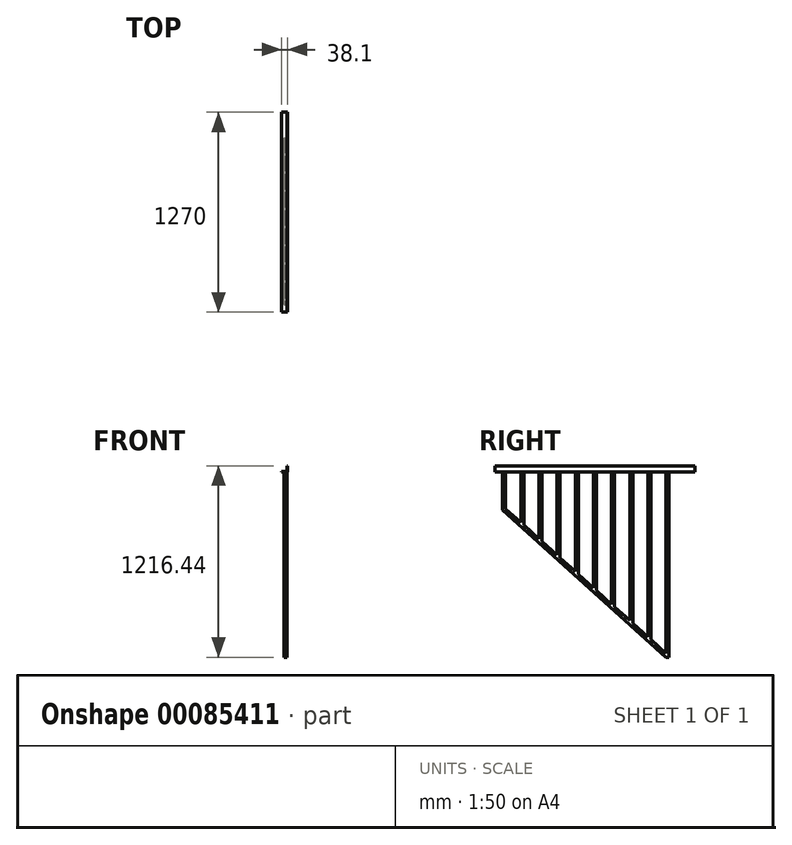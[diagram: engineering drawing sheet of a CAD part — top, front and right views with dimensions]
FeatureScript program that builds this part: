
annotation { "Feature Type Name" : "Feature", "Feature Type Description" : "" }
export const myFeature = defineFeature(function(context is Context, id is Id, definition is map)
    precondition{}
    {
        {
            var Q0;
            Q0=qCreatedBy(makeId("Right.planeOp"),FACE);
            var sketch = newSketch(context, id + "F2", { "sketchPlane" : qUnion([Q0])});
            skLineSegment(sketch, "E0", {"start": v(-1015.88, 696.31) * mm, "end": v(-1015.88, 601.06) * mm});
            skLineSegment(sketch, "E1", {"start": v(-1015.88, 601.06) * mm, "end": v(-790.45, 601.06) * mm});
            skLineSegment(sketch, "E2", {"start": v(-790.45, 601.06) * mm, "end": v(-790.45, 601.06) * mm});
            skLineSegment(sketch, "E3", {"start": v(-790.45, 601.06) * mm, "end": v(-790.45, 397.86) * mm});
            skLineSegment(sketch, "E4", {"start": v(-790.45, 397.86) * mm, "end": v(-565.03, 397.86) * mm});
            skLineSegment(sketch, "E5", {"start": v(-565.03, 397.86) * mm, "end": v(-565.03, 194.66) * mm});
            skLineSegment(sketch, "E6", {"start": v(-565.03, 194.66) * mm, "end": v(-339.6, 194.66) * mm});
            skLineSegment(sketch, "E7", {"start": v(-339.6, 194.66) * mm, "end": v(-339.6, -14.89) * mm});
            skLineSegment(sketch, "E8", {"start": v(-339.6, -14.89) * mm, "end": v(-339.6, -14.89) * mm});
            skLineSegment(sketch, "E9", {"start": v(-114.18, -14.89) * mm, "end": v(-339.6, -14.89) * mm});
            skLineSegment(sketch, "E10", {"start": v(-114.18, -14.89) * mm, "end": v(-114.18, -218.09) * mm});
            skLineSegment(sketch, "E11", {"start": v(-114.18, -218.09) * mm, "end": v(114.42, -218.09) * mm});
            skLineSegment(sketch, "E12", {"start": v(114.42, -218.09) * mm, "end": v(114.42, -421.29) * mm});
            skLineSegment(sketch, "E13", {"start": v(114.42, -421.29) * mm, "end": v(343.02, -421.29) * mm});
            skLineSegment(sketch, "E14", {"start": v(-1015.88, 696.31) * mm, "end": v(1087.24, 696.31) * mm});
            skLineSegment(sketch, "E15", {"start": v(343.02, -421.29) * mm, "end": v(343.02, -624.49) * mm});
            skLineSegment(sketch, "E16", {"start": v(343.02, -624.49) * mm, "end": v(571.62, -624.49) * mm});
            skLineSegment(sketch, "E17", {"start": v(571.62, -624.49) * mm, "end": v(571.62, -827.69) * mm});
            skLineSegment(sketch, "E18", {"start": v(571.62, -827.69) * mm, "end": v(806.57, -827.69) * mm});
            skLineSegment(sketch, "E19", {"start": v(806.57, -827.69) * mm, "end": v(806.57, -1030.89) * mm});
            skLineSegment(sketch, "E20", {"start": v(806.57, -1030.89) * mm, "end": v(1035.17, -1030.89) * mm});
            skLineSegment(sketch, "E21", {"start": v(774.82, -827.69) * mm, "end": v(774.82, 696.31) * mm});
            skLineSegment(sketch, "E22", {"start": v(863.72, 696.31) * mm, "end": v(863.72, -1030.89) * mm});
            skLineSegment(sketch, "E23", {"start": v(1035.17, -1030.89) * mm, "end": v(1035.17, -1234.09) * mm});
            skLineSegment(sketch, "E24", {"start": v(1035.17, -1234.09) * mm, "end": v(1503, -1234.09) * mm});
            skLineSegment(sketch, "E25", {"start": v(806.57, -827.69) * mm, "end": v(1035.17, -1030.89) * mm, "construction": true});
            skLineSegment(sketch, "E26", {"start": v(971.74, -1030.89) * mm, "end": v(806.57, -884.07) * mm, "construction": true});
            skCircle(sketch, "E27", {"center": v(857.37, -980.09) * mm, "radius": 50.8 * mm, "construction": true});
            skLineSegment(sketch, "E28", {"start": v(806.57, -1030.89) * mm, "end": v(893.3, -944.17) * mm, "construction": true});
            skSolve(sketch);
        }
        {
            var Q0;
            Q0=qCreatedBy(makeId("Front.planeOp"),FACE);
            var sketch = newSketch(context, id + "F0", { "sketchPlane" : qUnion([Q0])});
            skLineSegment(sketch, "E29", {"start": v(3.17, 731.24) * mm, "end": v(3.18, 693.14) * mm});
            skLineSegment(sketch, "E30", {"start": v(3.18, 693.14) * mm, "end": v(-34.93, 693.14) * mm});
            skLineSegment(sketch, "E31", {"start": v(-34.93, 693.14) * mm, "end": v(-34.93, 696.31) * mm});
            skLineSegment(sketch, "E32", {"start": v(-34.93, 696.31) * mm, "end": v(0, 696.31) * mm});
            skLineSegment(sketch, "E33", {"start": v(0, 696.31) * mm, "end": v(0, 731.24) * mm});
            skLineSegment(sketch, "E34", {"start": v(0, 731.24) * mm, "end": v(3.17, 731.24) * mm});
            skSolve(sketch);
        }
        {
            var Q0;
            Q0=makeQuery(id+"F0.imprint","IMPRINT",FACE,{"disambiguationData":[TD([[makeQuery(id+"F0.imprint","IMPRINT",EDGE,{"derivedFrom":sQuery(id+"F0.wireOp",EDGE,"E29")}),-1.0]])]});
            extrude(context, id + "F1", {"entities" : qUnion([Q0]), "depth" : 762 * mm, "hasSecondDirection" : true, "secondDirectionOppositeDirection" : true, "secondDirectionDepth" : 508 * mm});
        }
        {
            var Q0;
            Q0=qCreatedBy(makeId("Right.planeOp"),FACE);
            var sketch = newSketch(context, id + "F3", { "sketchPlane" : qUnion([Q0])});
            skLineSegment(sketch, "E35", {"start": v(806.57, -1030.89) * mm, "end": v(1035.17, -1234.09) * mm});
            skPoint(sketch, "E36", {"position": v(806.57, -1030.89) * mm});
            skLineSegment(sketch, "E37", {"start": v(-714.25, 693.14) * mm, "end": v(-714.25, 449.2) * mm});
            skLineSegment(sketch, "E38", {"start": v(-695.2, 693.14) * mm, "end": v(-695.2, 457.69) * mm});
            skLineSegment(sketch, "E39", {"start": v(-598.9, 693.14) * mm, "end": v(-598.9, 371.01) * mm});
            skLineSegment(sketch, "E40", {"start": v(-579.84, 693.14) * mm, "end": v(-579.84, 353.87) * mm});
            skLineSegment(sketch, "E41", {"start": v(-368.18, 693.14) * mm, "end": v(-368.18, 163.37) * mm});
            skLineSegment(sketch, "E42", {"start": v(-349.13, 693.14) * mm, "end": v(-349.13, 146.22) * mm});
            skLineSegment(sketch, "E43", {"start": v(-483.54, 693.14) * mm, "end": v(-483.54, 267.19) * mm});
            skLineSegment(sketch, "E44", {"start": v(-464.49, 693.14) * mm, "end": v(-464.49, 250.04) * mm});
            skLineSegment(sketch, "E45", {"start": v(-252.82, 693.14) * mm, "end": v(-252.82, 59.54) * mm});
            skLineSegment(sketch, "E46", {"start": v(-233.77, 693.14) * mm, "end": v(-233.77, 42.4) * mm});
            skLineSegment(sketch, "E47", {"start": v(-137.46, 693.14) * mm, "end": v(-137.46, -44.28) * mm});
            skLineSegment(sketch, "E48", {"start": v(-118.41, 693.14) * mm, "end": v(-118.41, -61.42) * mm});
            skLineSegment(sketch, "E49", {"start": v(-22.1, 693.14) * mm, "end": v(-22.1, -148.1) * mm});
            skLineSegment(sketch, "E50", {"start": v(-3.05, 693.14) * mm, "end": v(-3.05, -165.25) * mm});
            skLineSegment(sketch, "E51", {"start": v(93.26, 693.14) * mm, "end": v(93.26, -251.92) * mm});
            skLineSegment(sketch, "E52", {"start": v(112.3, 693.14) * mm, "end": v(112.3, -269.07) * mm});
            skLineSegment(sketch, "E53", {"start": v(208.61, 693.14) * mm, "end": v(208.61, -355.75) * mm});
            skLineSegment(sketch, "E54", {"start": v(227.66, 693.14) * mm, "end": v(227.66, -372.9) * mm});
            skLineSegment(sketch, "E55", {"start": v(323.97, 693.14) * mm, "end": v(323.97, -459.57) * mm});
            skLineSegment(sketch, "E56", {"start": v(343.02, 693.14) * mm, "end": v(343.02, -485.2) * mm});
            skLineSegment(sketch, "E57.trimOffspring", {"start": v(343.02, 693.14) * mm, "end": v(323.97, 693.14) * mm});
            skLineSegment(sketch, "E58.trimOffspring", {"start": v(227.66, 693.14) * mm, "end": v(208.61, 693.14) * mm});
            skLineSegment(sketch, "E59.trimOffspring", {"start": v(112.3, 693.14) * mm, "end": v(93.26, 693.14) * mm});
            skLineSegment(sketch, "E60.trimOffspring", {"start": v(-3.05, 693.14) * mm, "end": v(-22.1, 693.14) * mm});
            skLineSegment(sketch, "E61.trimOffspring", {"start": v(-118.41, 693.14) * mm, "end": v(-137.46, 693.14) * mm});
            skLineSegment(sketch, "E62.trimOffspring", {"start": v(-233.77, 693.14) * mm, "end": v(-252.82, 693.14) * mm});
            skLineSegment(sketch, "E63.trimOffspring", {"start": v(-349.13, 693.14) * mm, "end": v(-368.18, 693.14) * mm});
            skLineSegment(sketch, "E64.trimOffspring", {"start": v(-464.49, 693.14) * mm, "end": v(-483.54, 693.14) * mm});
            skLineSegment(sketch, "E65", {"start": v(-1015.88, 601.06) * mm, "end": v(571.62, -827.69) * mm, "construction": true});
            skLineSegment(sketch, "E66", {"start": v(323.97, -459.57) * mm, "end": v(227.66, -372.9) * mm});
            skLineSegment(sketch, "E67", {"start": v(208.61, -355.75) * mm, "end": v(112.3, -269.07) * mm});
            skLineSegment(sketch, "E68", {"start": v(93.26, -251.92) * mm, "end": v(-3.05, -165.25) * mm});
            skLineSegment(sketch, "E69", {"start": v(-22.1, -148.1) * mm, "end": v(-118.41, -61.42) * mm});
            skLineSegment(sketch, "E70", {"start": v(-137.46, -44.28) * mm, "end": v(-233.77, 42.4) * mm});
            skLineSegment(sketch, "E71", {"start": v(-252.82, 59.54) * mm, "end": v(-349.13, 146.22) * mm});
            skLineSegment(sketch, "E72", {"start": v(-368.18, 163.37) * mm, "end": v(-464.49, 250.04) * mm});
            skLineSegment(sketch, "E73", {"start": v(-483.54, 267.19) * mm, "end": v(-579.84, 353.87) * mm});
            skLineSegment(sketch, "E74", {"start": v(-598.9, 371.01) * mm, "end": v(-695.2, 457.69) * mm});
            skLineSegment(sketch, "E75", {"start": v(-714.25, 449.2) * mm, "end": v(323.97, -485.2) * mm});
            skCircle(sketch, "E76", {"center": v(-635.23, 139.87) * mm, "radius": 50.8 * mm});
            skLineSegment(sketch, "E77", {"start": v(323.97, -459.57) * mm, "end": v(323.97, -485.2) * mm, "construction": true});
            skLineSegment(sketch, "E78", {"start": v(323.97, -485.2) * mm, "end": v(343.02, -485.2) * mm});
            skLineSegment(sketch, "E79.trimOffspring", {"start": v(-579.84, 693.14) * mm, "end": v(-598.9, 693.14) * mm});
            skLineSegment(sketch, "E80.trimOffspring", {"start": v(-695.2, 693.14) * mm, "end": v(-714.25, 693.14) * mm});
            skLineSegment(sketch, "E81", {"start": v(-695.2, 457.69) * mm, "end": v(-714.25, 449.2) * mm, "construction": true});
            skSolve(sketch);
        }
        {
            var Q0;
            {var subQ1=sQuery(id+"F3.wireOp",EDGE,"E37");Q0=makeQuery(id+"F3.imprint","IMPRINT",FACE,{"disambiguationData":[TD([[makeQuery(id+"F3.imprint","IMPRINT",EDGE,{"derivedFrom":subQ1}),1.0]])]});}
            extrude(context, id + "F4", {"entities" : qUnion([Q0]), "operationType" : NewBodyOperationType.ADD, "oppositeDirection" : true, "depth" : 19.05 * mm});
        }
    });
